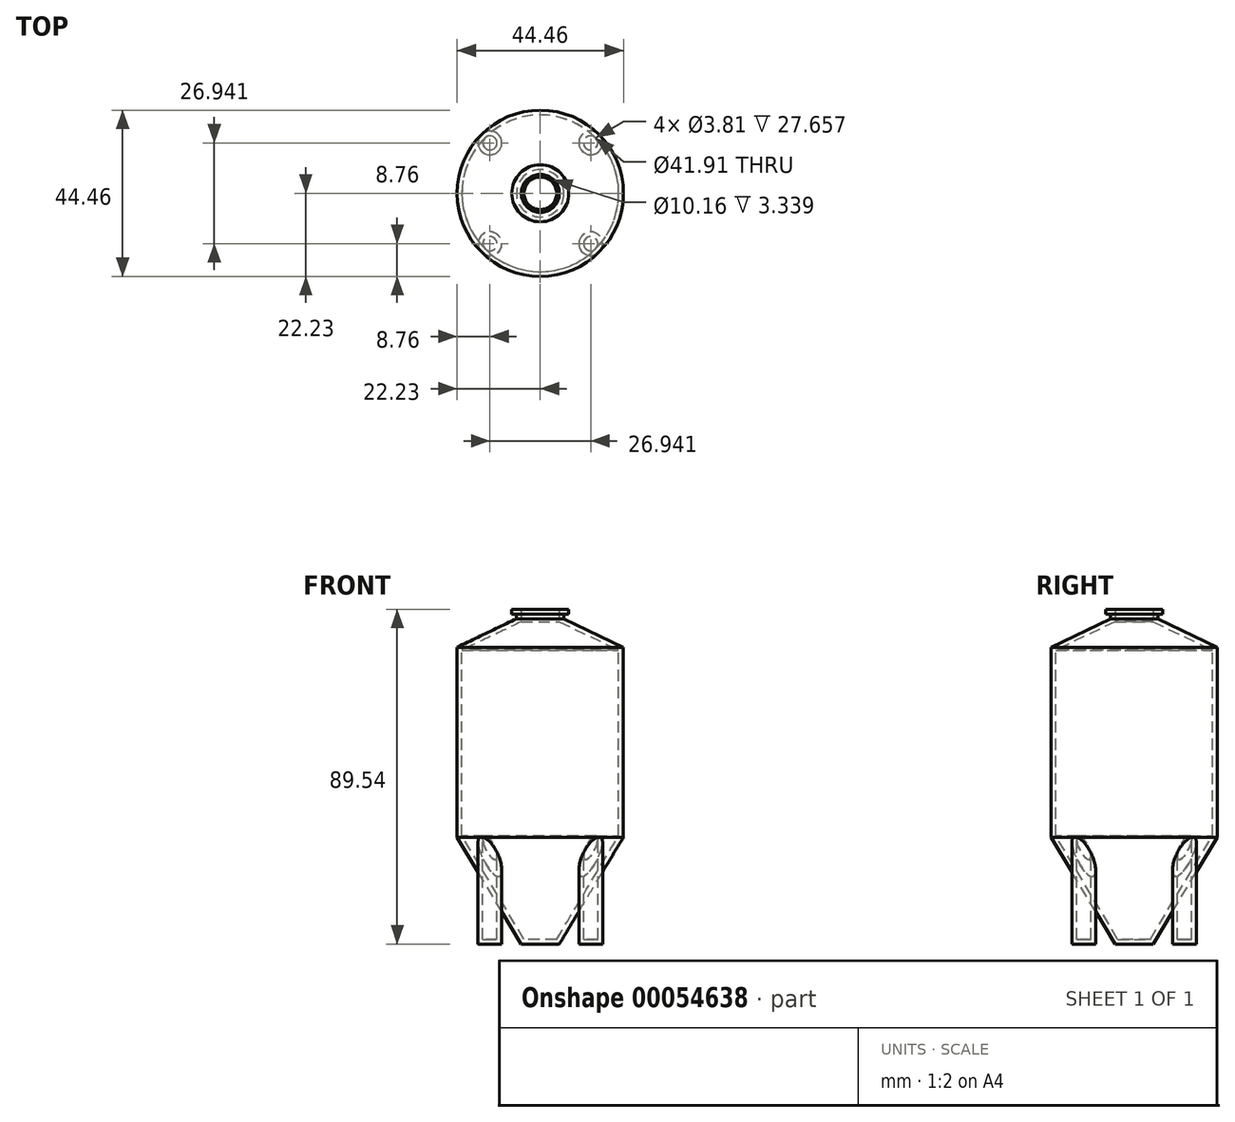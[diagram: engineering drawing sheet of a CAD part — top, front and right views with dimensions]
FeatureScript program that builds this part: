
annotation { "Feature Type Name" : "Feature", "Feature Type Description" : "" }
export const myFeature = defineFeature(function(context is Context, id is Id, definition is map)
    precondition{}
    {
        {
            var Q0;
            Q0=qCreatedBy(makeId("Top.planeOp"),FACE);
            var sketch = newSketch(context, id + "F0", { "sketchPlane" : qUnion([Q0])});
            skCircle(sketch, "E0", {"center": v(0, 0) * mm, "radius": 22.23 * mm});
            skSolve(sketch);
        }
        {
            var Q0;
            Q0=makeQuery(id+"F0.imprint","IMPRINT",FACE,{"disambiguationData":[TD([[makeQuery(id+"F0.imprint","IMPRINT",EDGE,{"derivedFrom":sQuery(id+"F0.wireOp",EDGE,"E0")}),1.0]])]});
            extrude(context, id + "F1", {"entities" : qUnion([Q0]), "oppositeDirection" : true, "depth" : 50.8 * mm});
        }
        {
            var Q0;
            Q0=qCreatedBy(makeId("Front.planeOp"),FACE);
            var sketch = newSketch(context, id + "F2", { "sketchPlane" : qUnion([Q0])});
            skLineSegment(sketch, "E1", {"start": v(22.23, -50.8) * mm, "end": v(5.08, -79.38) * mm});
            skLineSegment(sketch, "E2", {"start": v(5.08, -79.38) * mm, "end": v(0, -79.38) * mm});
            skLineSegment(sketch, "E3", {"start": v(0, -79.38) * mm, "end": v(0, -50.8) * mm});
            skLineSegment(sketch, "E4", {"start": v(0, -50.8) * mm, "end": v(22.23, -50.8) * mm});
            skSolve(sketch);
        }
        {
            var Q0;
            Q0=makeQuery(id+"F1.opExtrude","CAP_FACE",FACE,{"disambiguationData":[OSD([sQuery(id+"F0.wireOp",EDGE,"E0")])],"isStart":false});
            var sketch = newSketch(context, id + "F3", { "sketchPlane" : qUnion([Q0])});
            skCircle(sketch, "E5", {"center": v(-13.47, 13.47) * mm, "radius": 3.18 * mm});
            skCircle(sketch, "E6", {"center": v(13.47, 13.47) * mm, "radius": 3.18 * mm});
            skCircle(sketch, "E7", {"center": v(13.47, -13.47) * mm, "radius": 3.18 * mm});
            skCircle(sketch, "E8", {"center": v(-13.47, -13.47) * mm, "radius": 3.18 * mm});
            skLineSegment(sketch, "E9.rect.bottom", {"start": v(-15.72, 15.72) * mm, "end": v(15.72, 15.72) * mm, "construction": true});
            skLineSegment(sketch, "E9.rect.top", {"start": v(-15.72, -15.72) * mm, "end": v(15.72, -15.72) * mm, "construction": true});
            skLineSegment(sketch, "E9.rect.left", {"start": v(-15.72, 15.72) * mm, "end": v(-15.72, -15.72) * mm, "construction": true});
            skLineSegment(sketch, "E9.rect.right", {"start": v(15.72, 15.72) * mm, "end": v(15.72, -15.72) * mm, "construction": true});
            skPoint(sketch, "E9.rect.middle", {"position": v(0, 0) * mm});
            skSolve(sketch);
        }
        {
            var Q0;
            Q0=qSketchRegion(id+"F3",true);
            extrude(context, id + "F4", {"entities" : qUnion([Q0]), "operationType" : NewBodyOperationType.ADD, "depth" : 28.57 * mm});
        }
        {
            var Q0;
            Q0=qSketchRegion(id+"F2",true);
            var Q1;
            Q1=makeQuery(id+"F1.opExtrude","SWEPT_FACE",FACE,{"disambiguationData":[OSD([sQuery(id+"F0.wireOp",EDGE,"E0")])]});
            revolve(context, id + "F5", {"operationType" : NewBodyOperationType.ADD, "entities" : qUnion([Q0]), "axis" : qUnion([Q1]), "revolveType" : RevolveType.FULL});
        }
        {
            var Q0;
            Q0=qCreatedBy(makeId("Right.planeOp"),FACE);
            var sketch = newSketch(context, id + "F6", { "sketchPlane" : qUnion([Q0])});
            skLineSegment(sketch, "E10", {"start": v(0, 0) * mm, "end": v(-22.22, 0) * mm});
            skLineSegment(sketch, "E11", {"start": v(-22.23, 0) * mm, "end": v(-6.35, 7.62) * mm});
            skLineSegment(sketch, "E12", {"start": v(-6.35, 7.62) * mm, "end": v(-6.35, 8.9) * mm});
            skLineSegment(sketch, "E13", {"start": v(-6.35, 8.9) * mm, "end": v(-7.62, 8.9) * mm});
            skLineSegment(sketch, "E14", {"start": v(-7.62, 8.9) * mm, "end": v(-7.62, 10.16) * mm});
            skLineSegment(sketch, "E15", {"start": v(-7.62, 10.16) * mm, "end": v(0, 10.16) * mm});
            skLineSegment(sketch, "E16", {"start": v(0, 10.16) * mm, "end": v(0, 0) * mm});
            skSolve(sketch);
        }
        {
            var Q0;
            Q0=makeQuery(id+"F6.imprint","IMPRINT",FACE,{"disambiguationData":[TD([[makeQuery(id+"F6.imprint","IMPRINT",EDGE,{"derivedFrom":sQuery(id+"F6.wireOp",EDGE,"E10")}),-1.0]])]});
            var Q1;
            Q1=makeQuery(id+"F1.opExtrude","SWEPT_FACE",FACE,{"disambiguationData":[OSD([sQuery(id+"F0.wireOp",EDGE,"E0")])]});
            revolve(context, id + "F7", {"operationType" : NewBodyOperationType.ADD, "entities" : qUnion([Q0]), "axis" : qUnion([Q1]), "revolveType" : RevolveType.FULL});
        }
        {
            var Q0;
            Q0=makeQuery(id+"F7.opRevolve","SWEPT_FACE",FACE,{"disambiguationData":[OSD([sQuery(id+"F6.wireOp",EDGE,"E15")])]});
            var Q1;
            Q1=makeQuery(id+"F7.opRevolve","SWEPT_FACE",FACE,{"disambiguationData":[OSD([sQuery(id+"F6.wireOp",EDGE,"E10")])]});
            shell(context, id + "F8", {"entities" : qUnion([Q0, Q1]), "thickness" : 1.27 * mm});
        }
    });
